# Revit family: Shower_Set-GROHE-New_Tempesta_100-2759810E
name_source: partatom
category: Plumbing Fixtures
revit_build: Autodesk Revit 2014 (Build: 20130308_1515(x64)
units: mm (PartAtom-declared; Revit-internal decimal feet)

## types (1)
- 2759810E
    Assembly Code = D2010710
    CW Connection = Yes
    CWFU = 3
    CalGreen Compliant = Yes
    Cold Water Connection Diameter = 1/2"
    Cold Water Connection Radius = 1/4"
    Default Elevation = 74"
    Description = New Tempesta 100 Shower Rail Set 2 Sprays
    Finish = Metal-Grohe-10E-Chrome
    Flow Rate = 1.5 gpm (5.7 l/min)
    HW Connection = Yes
    HWFU = 3
    Hand Shower Geometry = 27597 Shower Handle : 27597 Hand Shower 10E
    Height = 24 7/16"
    Hot Water Connection Diameter = 1"
    Hot Water Connection Radius = 1/4"
    Installation Type = Wall Mounted
    Length = 3 3/16"
    Manufacturer = Grohe
    Material = Metal-Grohe-10E-Chrome
    Model = 2759810E
    Price = Prices may vary. Please consult Manufacturer Representative for most up-to-date price list.
    Product Page URL = https://www.grohe.us
    Tempered Connection Diameter = 1/2"
    Tempered Connection Radius = 1/4"
    URL = https://www.grohe.com
    Vent Connection = No
    WFU = 4
    Warranty Documentation Link = https://cdn.cloud.grohe.com
    Waste Connection = No
    Width = 2 7/8"
    cUPC Compliant = Yes

## geometry (parser evidence)
native form markers: Sweep x4
no freeform markers — native parametric forms only
